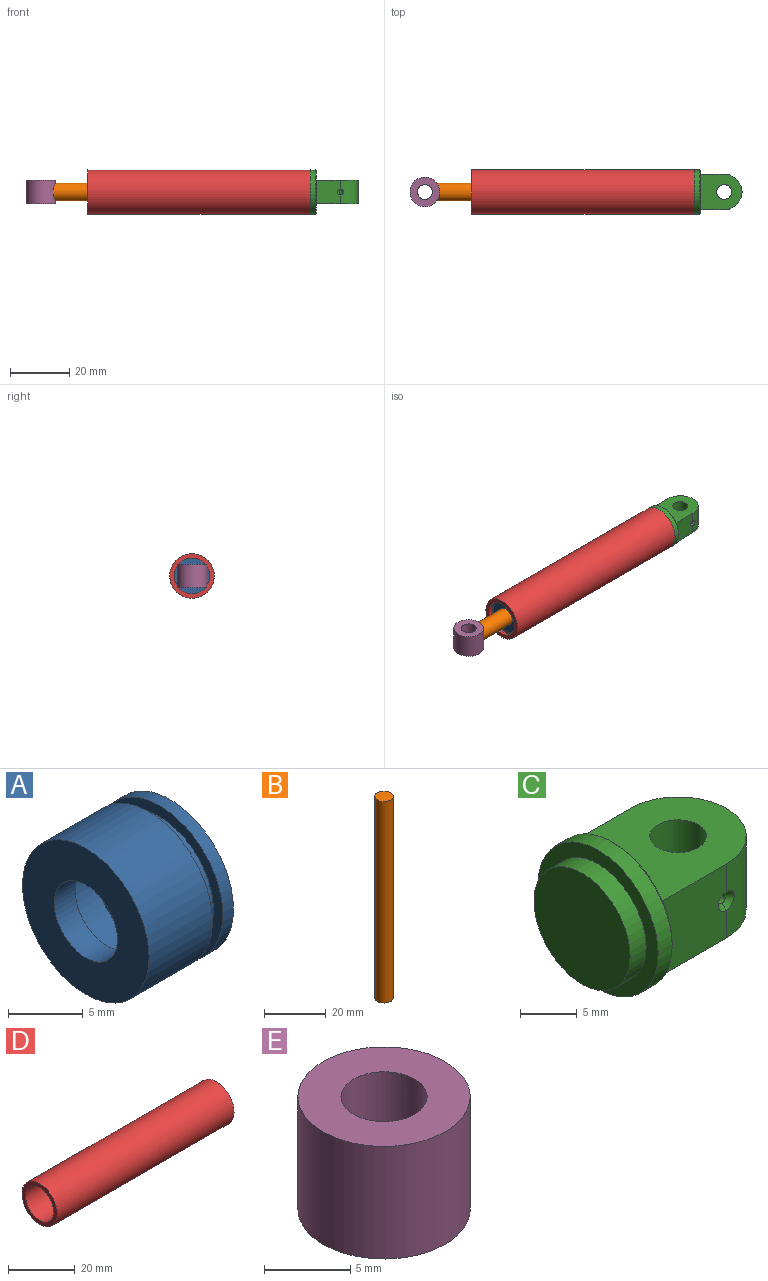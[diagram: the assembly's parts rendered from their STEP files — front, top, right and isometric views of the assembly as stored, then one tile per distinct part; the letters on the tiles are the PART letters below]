
ASSEMBLY  parts=5 mates=4
PART A: 12 faces, bbox 8x12x12 mm
  f0: cylinder r=3mm len=6mm, axis (1,0,0), area 56.5mm2, adj f1,f11
  f1: plane 12x12mm, normal (1,0,0), area 84.8mm2, adj f0,f2
  f2: cylinder r=6mm len=12mm, axis (1,0,0), area 37.7mm2, adj f1,f3
  f3: plane 12x12mm, normal (-1,0,0), area 31.4mm2, adj f2,f4
  f4: cylinder r=5.1mm len=10.2mm, axis (1,0,0), area 32mm2, adj f3,f5
  f5: plane 12x12mm, normal (1,0,0), area 31.4mm2, adj f4,f6
  f6: cylinder r=6mm len=12mm, axis (1,0,0), area 226.2mm2, adj f5,f7
  f7: plane 12x12mm, normal (-1,0,0), area 84.8mm2, adj f6,f8
  f8: cylinder r=3mm len=6mm, axis (1,0,0), area 37.7mm2, adj f7,f9
  f9: plane 8.5x8.5mm, normal (1,0,0), area 28.5mm2, adj f8,f10
  f10: cylinder r=4.25mm len=8.5mm, axis (1,0,0), area 80.1mm2, adj f9,f11
  f11: plane 8.5x8.5mm, normal (-1,0,0), area 28.5mm2, adj f0,f10
PART B: 3 faces, bbox 6x6x80 mm
  f0: cylinder r=3mm len=80mm, axis (0,0,-1), area 1508mm2, adj f1,f2
  f1: plane 6x6mm, normal (0,0,1), area 28.3mm2, adj f0
  f2: plane 6x6mm, normal (0,0,-1), area 28.3mm2, adj f0
PART C: 15 faces, bbox 18x15x15 mm
  f0: cylinder r=7.5mm len=15mm, axis (1,0,0), area 82.5mm2, adj f1,f14
  f1: plane 15x15mm, normal (-1,0,0), area 63.6mm2, adj f0,f3
  f2: plane 14.5x14.5mm, normal (1,0,0), area 69.1mm2, adj f5,f6,f9,f10,f14
  f3: cylinder r=6mm len=12mm, axis (1,0,0), area 75.4mm2, adj f1,f4
  f4: plane 12x12mm, normal (-1,0,0), area 113.1mm2, adj f3
  f5: plane 8x8mm, normal (0,1,0), area 64mm2, adj f2,f7,f9,f10
  f6: plane 8x8mm, normal (0,-1,0), area 62.4mm2, adj f2,f7,f9,f10,f13
  f7: cylinder r=6mm len=12mm, axis (0,0,-1), area 149.1mm2, adj f5,f6,f9,f10,f12
  f8: cylinder r=2.5mm len=8mm, axis (0,0,-1), area 124.9mm2, adj f9,f10,f11
  f9: plane 14x12mm, normal (0,0,1), area 132.9mm2, adj f2,f5,f6,f7,f8
  f10: plane 14x12mm, normal (0,0,-1), area 132.9mm2, adj f2,f5,f6,f7,f8
  f11: cylinder r=0.5mm len=3.05mm, axis (0,-1,0), area 9.5mm2, adj f8,f12,f13
  f12: bspline ~2x1.09mm, area 1.8mm2, adj f7,f11,f13
  f13: cone r=0.5mm half-angle=45deg, axis (0,-1,0), area 1.7mm2, adj f6,f11,f12
  f14: cone r=7.25mm half-angle=45deg, axis (-1,0,0), area 16.4mm2, adj f0,f2
PART D: 12 faces, bbox 75x15x15 mm
  f0: cylinder r=6mm len=12mm, axis (-1,0,0), area 301.6mm2, adj f1,f11
  f1: plane 13x13mm, normal (1,0,0), area 19.6mm2, adj f0,f2
  f2: cylinder r=6.5mm len=13mm, axis (-1,0,0), area 40.8mm2, adj f1,f3
  f3: plane 13x13mm, normal (-1,0,0), area 19.6mm2, adj f2,f4
  f4: cylinder r=6mm len=12mm, axis (-1,0,0), area 37.7mm2, adj f3,f5
  f5: plane 15x15mm, normal (1,0,0), area 63.6mm2, adj f4,f6
  f6: cylinder r=7.5mm len=75mm, axis (-1,0,0), area 3534.3mm2, adj f5,f7
  f7: plane 15x15mm, normal (-1,0,0), area 63.6mm2, adj f6,f8
  f8: cylinder r=6mm len=64mm, axis (-1,0,0), area 2412.7mm2, adj f7,f9
  f9: plane 13x13mm, normal (1,0,0), area 19.6mm2, adj f8,f10
  f10: cylinder r=6.5mm len=13mm, axis (-1,0,0), area 40.8mm2, adj f9,f11
  f11: plane 13x13mm, normal (-1,0,0), area 19.6mm2, adj f0,f10
PART E: 8 faces, bbox 10x10x8 mm
  f0: cylinder r=5mm len=10mm, axis (0,0,-1), area 219.8mm2, adj f2,f3,f4,f7
  f1: cylinder r=2.5mm len=8mm, axis (0,0,-1), area 124.9mm2, adj f2,f3,f6
  f2: plane 10x10mm, normal (0,0,1), area 58.9mm2, adj f0,f1
  f3: plane 10x10mm, normal (0,0,-1), area 58.9mm2, adj f0,f1
  f4: cylinder r=3mm len=6mm, axis (0,1,0), area 19.1mm2, adj f0,f5
  f5: plane 6x6mm, normal (0,1,0), area 28.3mm2, adj f4
  f6: cylinder r=0.5mm len=2.25mm, axis (1,0,0), area 7.1mm2, adj f1,f7
  f7: bspline ~1.58x1.5mm, area 1.5mm2, adj f0,f6
PLACE A t=(-13.24,6.03,53.31)mm
PLACE B rot(axis=(0,1,0),90deg) t=(-35.45,6.03,53.31)mm
PLACE C t=(53.76,6.03,53.31)mm
PLACE D rot(axis=(0,1,0),180deg) t=(51.76,6.03,53.31)mm
PLACE E rot(axis=(0.71,0.71,0),180deg) t=(-38.95,6.03,57.31)mm
MATE fastened E.f4 <-> B.f0  axis (1,0,0) through (-35.45,6.03,53.31)mm
MATE fastened A.f0 <-> D.f0  axis (-1,0,0) through (-21.24,6.03,53.31)mm
MATE fastened C.f0 <-> D.f0  axis (-1,0,0) through (51.76,6.03,53.31)mm
MATE slider A.f0 <-> B.f0  axis (-1,0,0) through (-21.24,6.03,53.31)mm
